# Revit family: Shower-Showerarm-KALLISTA-Guise-P34250_1
name_source: partatom
category: Plumbing Fixtures
units: mm (PartAtom-declared; Revit-internal decimal feet)

## family parameters
Cut with Voids When Loaded = No
Host = Face
OmniClass Number = 23.31.25.00
OmniClass Title = Toilet and Bath Specialties
Part Type = Normal
Room Calculation Point = No
Round Connector Dimension = Use Diameter
Shared = No

## types (5) — shared parameters
ADA Compliant = No
Assembly Code = D2010700
CW Connection = No
Cold Water Inlet = Cold Water Inlet
Date Modified = 07/09/2024
Default Elevation = 72"
Description = Modern Showerhead
Drain Included = No
Flow Rate = 2 GPM
HW Connection = Yes
Height = 6 3/8"
Hot Water Inlet = Hot Water Inlet
Length = 8 9/16"
Manufacturer = Kallista Co.
Master Format 2014 = 22 42 23
Master Format 2014 Name = Residential Showers
Material = Premium Metal Construction
Pressure = 45.00 psi
Product Name = Guise
Tempered Water Inlet = Tempered Water Inlet
URL = https://www.kallista.com
Vent Connection = No
Waste Connection = No
Waste Water Outlet = Waste Water Outlet
WaterSense Certified = No
Width = 5"

## per-type parameters (varying)
| type | Finish | Model | Type |
| BAF-Brushed French Gold | Kallista-Metal-BAF-Brushed_French_Gold | P34250-00-BAF | 1 |
| BN-Brushed Nickel | Kallista-Metal-BN-Brushed_Nickel | P34250-00-BN | 2 |
| CP-Chrome | Kallista-Metal-CP-Chrome | P34250-00-CP | 3 |
| PGP-Polished Graphite | Kallista-Metal-PGP-Polished_Graphite | P34250-00-PGP | 4 |
| SN-Polished Nickel | Kallista-Metal-SN-Polished_Nickel | P34250-00-SN | 5 |

## geometry (parser evidence)
native form markers: Sweep x5
no freeform markers — native parametric forms only
